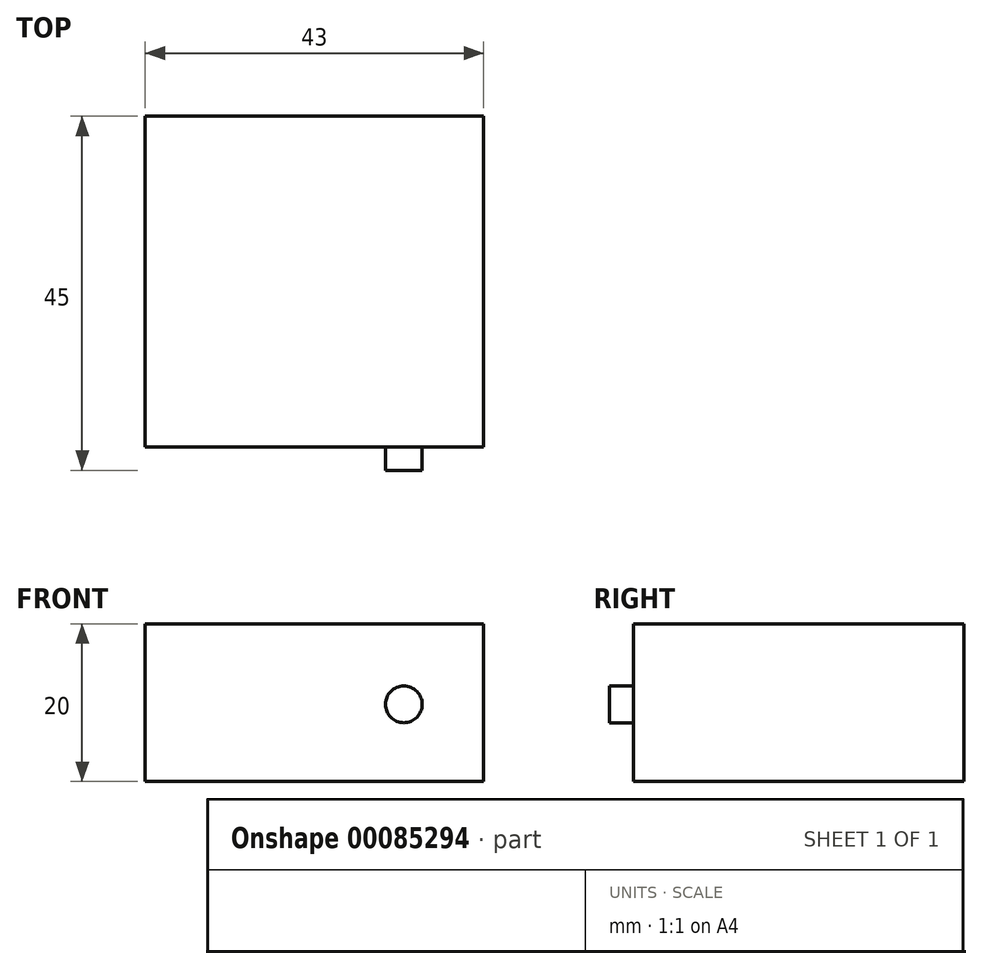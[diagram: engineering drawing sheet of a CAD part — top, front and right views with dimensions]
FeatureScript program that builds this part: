
annotation { "Feature Type Name" : "Feature", "Feature Type Description" : "" }
export const myFeature = defineFeature(function(context is Context, id is Id, definition is map)
    precondition{}
    {
        {
            var Q0;
            Q0=qCreatedBy(makeId("Top.planeOp"),FACE);
            var sketch = newSketch(context, id + "F0", { "sketchPlane" : qUnion([Q0])});
            skLineSegment(sketch, "E0.bottom", {"start": v(21.5, -21) * mm, "end": v(-21.5, -21) * mm});
            skLineSegment(sketch, "E0.top", {"start": v(21.5, 21) * mm, "end": v(-21.5, 21) * mm});
            skLineSegment(sketch, "E0.left", {"start": v(21.5, -21) * mm, "end": v(21.5, 21) * mm});
            skLineSegment(sketch, "E0.right", {"start": v(-21.5, -21) * mm, "end": v(-21.5, 21) * mm});
            skPoint(sketch, "E0.middle", {"position": v(0, 0) * mm});
            skSolve(sketch);
        }
        {
            var Q0;
            Q0=makeQuery(id+"F0.imprint","IMPRINT",FACE,{"disambiguationData":[TD([[makeQuery(id+"F0.imprint","IMPRINT",EDGE,{"derivedFrom":sQuery(id+"F0.wireOp",EDGE,"E0.bottom")}),-1.0]])]});
            extrude(context, id + "F1", {"entities" : qUnion([Q0]), "depth" : 20 * mm});
        }
        {
            var Q0;
            Q0=makeQuery(id+"F1.opExtrude","SWEPT_FACE",FACE,{"disambiguationData":[OSD([sQuery(id+"F0.wireOp",EDGE,"E0.bottom")])]});
            var sketch = newSketch(context, id + "F2", { "sketchPlane" : qUnion([Q0])});
            skCircle(sketch, "E1", {"center": v(11.35, 9.78) * mm, "radius": 2.33 * mm});
            skSolve(sketch);
        }
        {
            var Q0;
            Q0=makeQuery(id+"F2.imprint","IMPRINT",FACE,{"disambiguationData":[TD([[makeQuery(id+"F2.imprint","IMPRINT",EDGE,{"derivedFrom":sQuery(id+"F2.wireOp",EDGE,"E1")}),1.0]])]});
            extrude(context, id + "F3", {"entities" : qUnion([Q0]), "operationType" : NewBodyOperationType.ADD, "depth" : 3 * mm});
        }
    });
